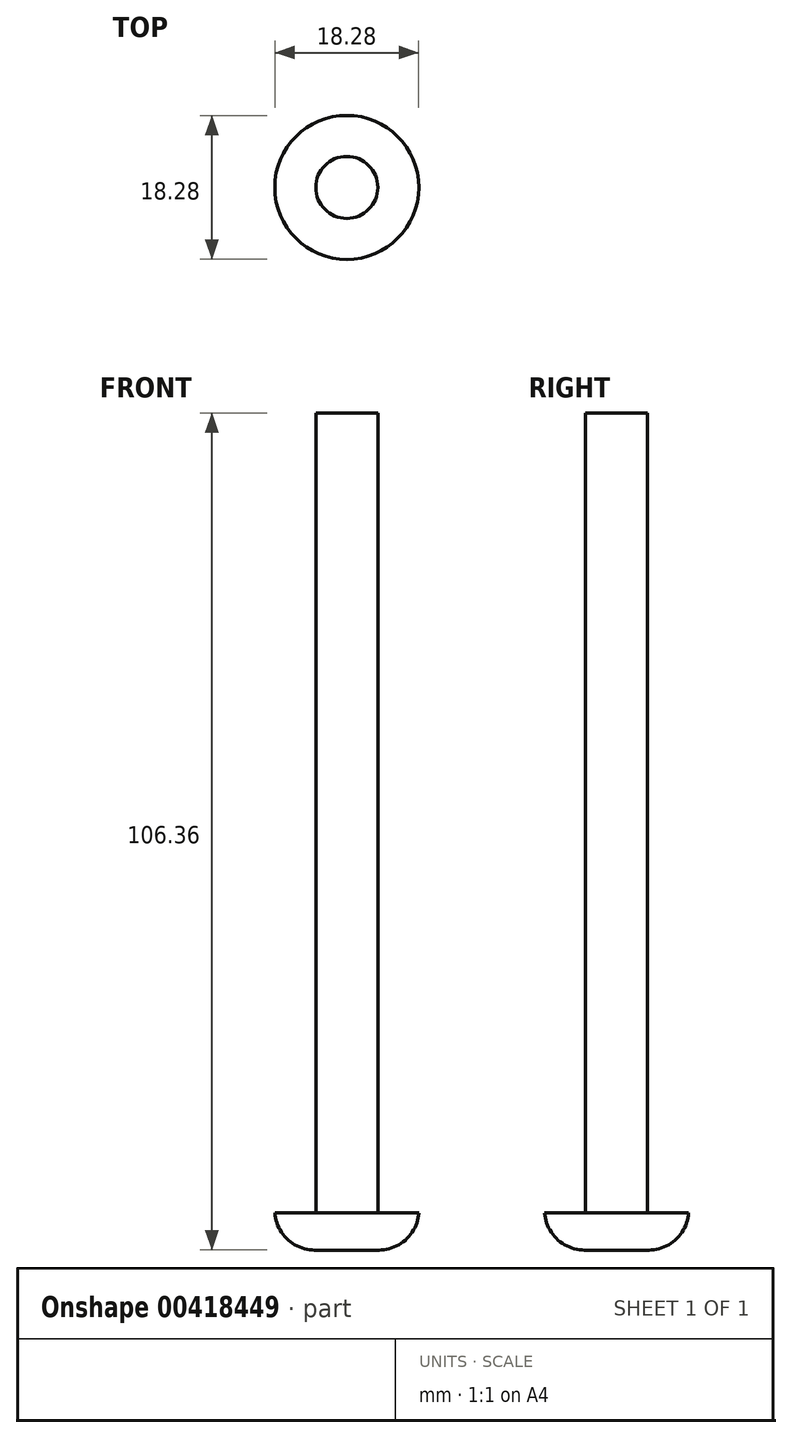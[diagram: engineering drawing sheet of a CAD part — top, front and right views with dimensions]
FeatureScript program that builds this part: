
annotation { "Feature Type Name" : "Feature", "Feature Type Description" : "" }
export const myFeature = defineFeature(function(context is Context, id is Id, definition is map)
    precondition{}
    {
        {
            var Q0;
            Q0=qCreatedBy(makeId("Top.planeOp"),FACE);
            var sketch = newSketch(context, id + "F0", { "sketchPlane" : qUnion([Q0])});
            skCircle(sketch, "E0", {"center": v(0, 0) * mm, "radius": 9.14 * mm});
            skCircle(sketch, "E1", {"center": v(0, 0) * mm, "radius": 3.94 * mm});
            skSolve(sketch);
        }
        {
            var Q0;
            Q0=makeQuery(id+"F0.imprint","IMPRINT",FACE,{"disambiguationData":[TD([[makeQuery(id+"F0.imprint","IMPRINT",EDGE,{"derivedFrom":sQuery(id+"F0.wireOp",EDGE,"E1")}),1.0]])]});
            extrude(context, id + "F1", {"entities" : qUnion([Q0]), "depth" : 101.6 * mm, "hasSecondDirection" : true, "secondDirectionOppositeDirection" : true, "secondDirectionDepth" : 2.54 * mm});
        }
        {
            var Q0;
            Q0=makeQuery(id+"F0.imprint","IMPRINT",FACE,{"disambiguationData":[TD([[makeQuery(id+"F0.imprint","IMPRINT",EDGE,{"derivedFrom":sQuery(id+"F0.wireOp",EDGE,"E0")}),1.0]])]});
            var Q1;
            Q1=makeQuery(id+"F0.imprint","IMPRINT",FACE,{"disambiguationData":[TD([[makeQuery(id+"F0.imprint","IMPRINT",EDGE,{"derivedFrom":sQuery(id+"F0.wireOp",EDGE,"E1")}),1.0]])]});
            extrude(context, id + "F2", {"entities" : qUnion([Q0, Q1]), "operationType" : NewBodyOperationType.ADD, "oppositeDirection" : true, "depth" : 4.76 * mm});
        }
        {
            var Q0;
            Q0=makeQuery(id+"F2.opExtrude","CAP_FACE",FACE,{"disambiguationData":[OSD([sQuery(id+"F0.wireOp",EDGE,"E0")])],"isStart":false});
            fillet(context, id + "F3", {"entities" : qUnion([Q0]), "radius" : 5.08 * mm, "tangentPropagation" : true, "allowEdgeOverflow" : false});
        }
    });
